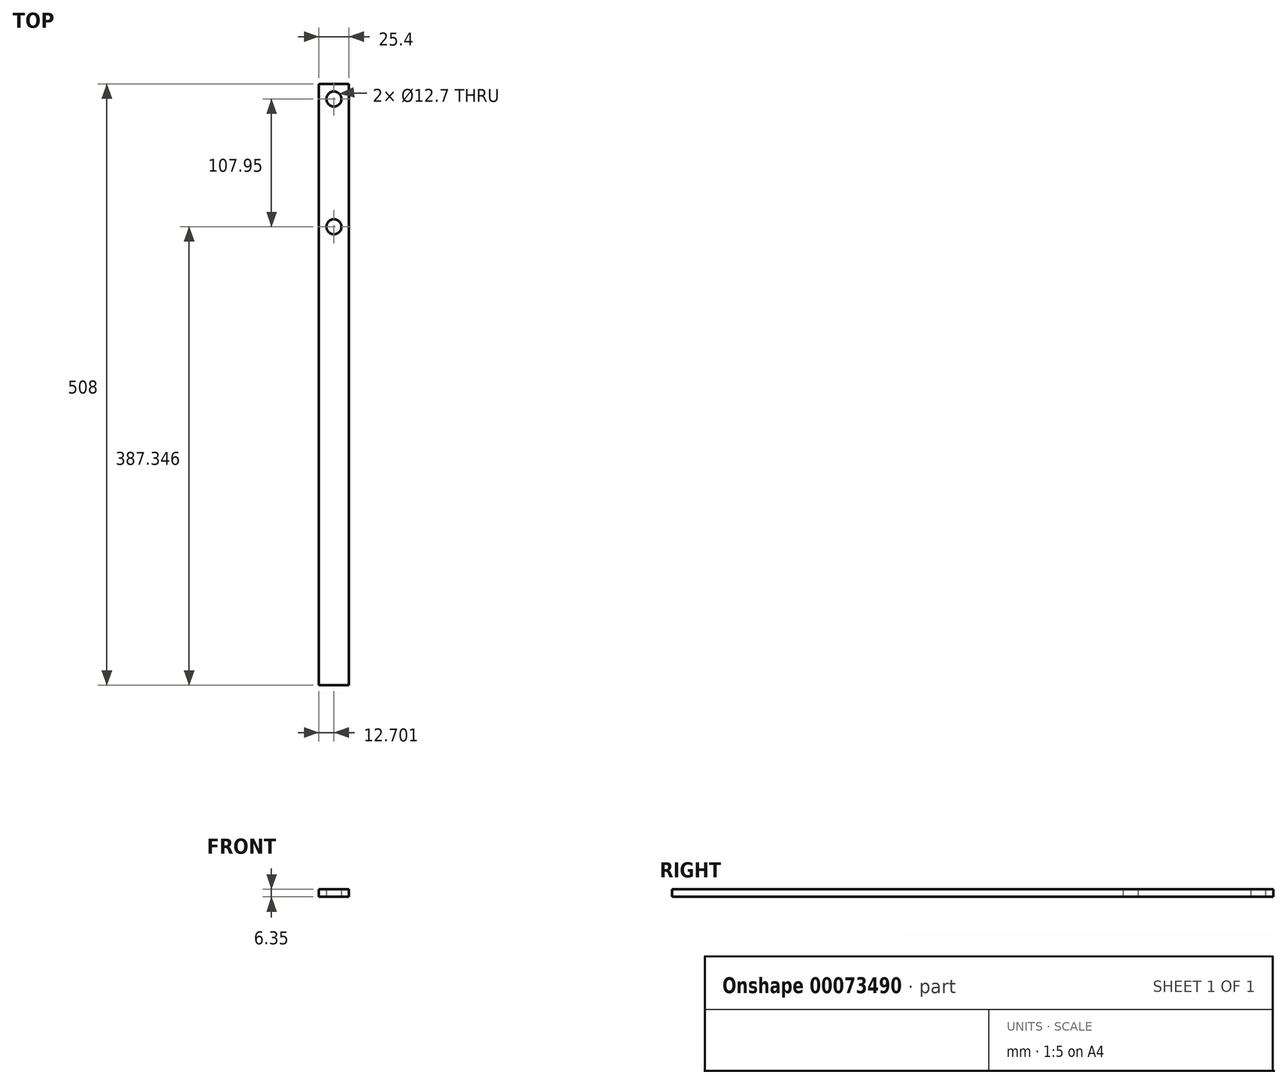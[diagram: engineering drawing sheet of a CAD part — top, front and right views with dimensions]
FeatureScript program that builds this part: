
annotation { "Feature Type Name" : "Feature", "Feature Type Description" : "" }
export const myFeature = defineFeature(function(context is Context, id is Id, definition is map)
    precondition{}
    {
        {
            var Q0;
            Q0=qCreatedBy(makeId("Top.planeOp"),FACE);
            var sketch = newSketch(context, id + "F0", { "sketchPlane" : qUnion([Q0])});
            skLineSegment(sketch, "E0.bottom", {"start": v(-14.18, -80.38) * mm, "end": v(11.22, -80.38) * mm});
            skLineSegment(sketch, "E0.top", {"start": v(-14.18, 427.62) * mm, "end": v(11.22, 427.62) * mm});
            skLineSegment(sketch, "E0.left", {"start": v(-14.18, -80.38) * mm, "end": v(-14.18, 427.62) * mm});
            skLineSegment(sketch, "E0.right", {"start": v(11.22, -80.38) * mm, "end": v(11.22, 427.62) * mm});
            skCircle(sketch, "E1", {"center": v(-1.48, 414.92) * mm, "radius": 6.35 * mm});
            skPoint(sketch, "E1.centerSnap0", {"position": v(-1.48, 427.62) * mm});
            skCircle(sketch, "E2", {"center": v(-1.48, 306.97) * mm, "radius": 6.35 * mm});
            skSolve(sketch);
        }
        {
            var Q0;
            Q0=makeQuery(id+"F0.imprint","IMPRINT",FACE,{"disambiguationData":[TD([[makeQuery(id+"F0.imprint","IMPRINT",EDGE,{"derivedFrom":sQuery(id+"F0.wireOp",EDGE,"E0.bottom")}),1.0]])]});
            extrude(context, id + "F1", {"entities" : qUnion([Q0]), "depth" : 6.35 * mm});
        }
    });
